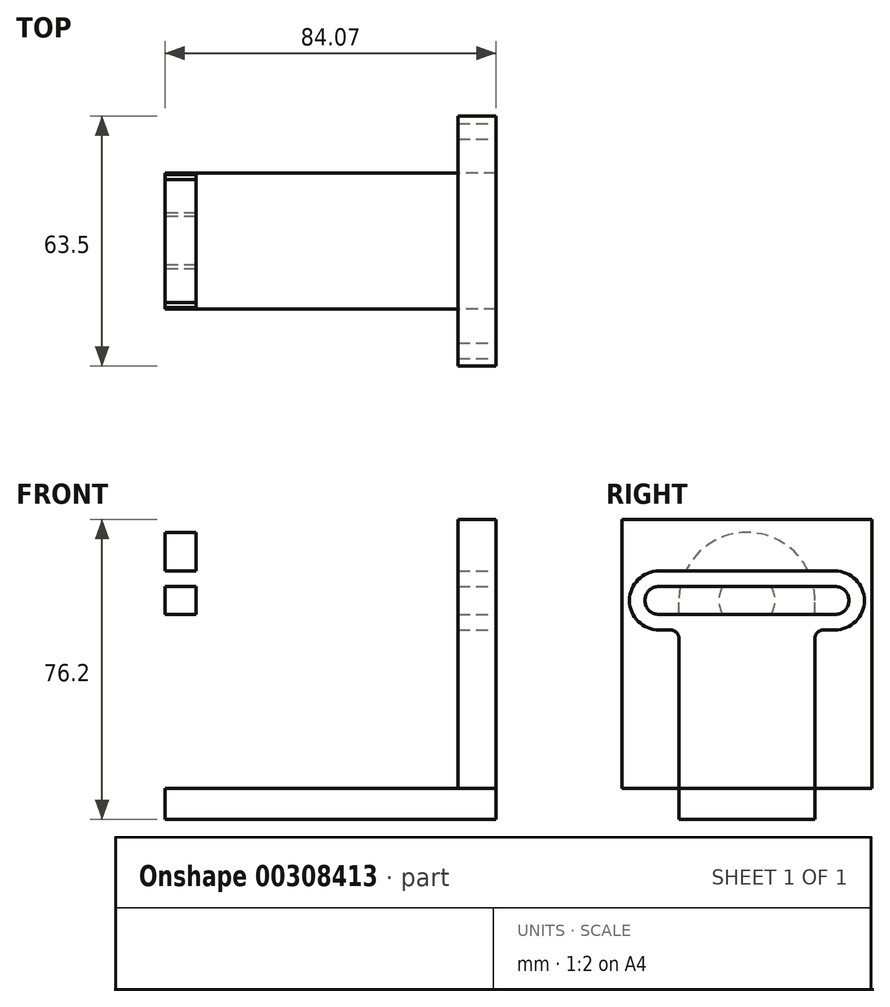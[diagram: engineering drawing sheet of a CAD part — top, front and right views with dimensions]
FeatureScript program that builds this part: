
annotation { "Feature Type Name" : "Feature", "Feature Type Description" : "" }
export const myFeature = defineFeature(function(context is Context, id is Id, definition is map)
    precondition{}
    {
        {
            var Q0;
            Q0=qCreatedBy(makeId("Front.planeOp"),FACE);
            var sketch = newSketch(context, id + "F0", { "sketchPlane" : qUnion([Q0])});
            skLineSegment(sketch, "E0.bottom", {"start": v(0, 0) * mm, "end": v(84.07, 0) * mm});
            skLineSegment(sketch, "E0.top", {"start": v(0, 76.2) * mm, "end": v(84.07, 76.2) * mm});
            skLineSegment(sketch, "E0.left", {"start": v(0, 0) * mm, "end": v(0, 76.2) * mm});
            skLineSegment(sketch, "E0.right", {"start": v(84.07, 0) * mm, "end": v(84.07, 76.2) * mm});
            skSolve(sketch);
        }
        {
            var Q0;
            Q0 = qSketchRegion(id + "F0", true);
            extrude(context, id + "F1", {"entities" : qUnion([Q0]), "oppositeDirection" : true, "depth" : 63.5 * mm});
        }
        {
            var Q0;
            Q0=makeQuery(id+"F1.opExtrude","CAP_FACE",FACE,{"disambiguationData":[OSD([sQuery(id+"F0.wireOp",EDGE,"E0.bottom"),sQuery(id+"F0.wireOp",EDGE,"E0.top"),sQuery(id+"F0.wireOp",EDGE,"E0.left"),sQuery(id+"F0.wireOp",EDGE,"E0.right")])],"isStart":true});
            var sketch = newSketch(context, id + "F2", { "sketchPlane" : qUnion([Q0])});
            skLineSegment(sketch, "E1", {"start": v(7.87, 76.2) * mm, "end": v(7.87, 7.87) * mm});
            skLineSegment(sketch, "E2", {"start": v(7.87, 7.87) * mm, "end": v(74.42, 7.87) * mm});
            skLineSegment(sketch, "E3", {"start": v(74.42, 7.87) * mm, "end": v(74.42, 76.2) * mm});
            skSolve(sketch);
        }
        {
            var Q0;
            {var subQ0=sQuery(id+"F2.wireOp",EDGE,"E1");Q0=makeQuery(id+"F2.imprint","IMPRINT",FACE,{"disambiguationData":[TD([[makeQuery(id+"F2.imprint","IMPRINT",EDGE,{"derivedFrom":subQ0}),1.0]])]});}
            extrude(context, id + "F3", {"entities" : qUnion([Q0]), "operationType" : NewBodyOperationType.REMOVE, "endBound" : BoundingType.THROUGH_ALL, "oppositeDirection" : true, "depth" : 25.4 * mm});
        }
        {
            var Q0;
            Q0=makeQuery(id+"F1.opExtrude","SWEPT_FACE",FACE,{"disambiguationData":[OSD([sQuery(id+"F0.wireOp",EDGE,"E0.left")])]});
            var sketch = newSketch(context, id + "F4", { "sketchPlane" : qUnion([Q0])});
            skLineSegment(sketch, "E4", {"start": v(-49.02, 7.87) * mm, "end": v(-14.48, 7.87) * mm});
            skLineSegment(sketch, "E5", {"start": v(-63.5, 7.87) * mm, "end": v(0, 7.87) * mm});
            skLineSegment(sketch, "E6", {"start": v(-31.75, 76.2) * mm, "end": v(-31.75, 7.87) * mm, "construction": true});
            skLineSegment(sketch, "E7", {"start": v(-49.02, 7.87) * mm, "end": v(-49.02, 55.63) * mm});
            skLineSegment(sketch, "E8", {"start": v(-14.48, 7.87) * mm, "end": v(-14.48, 55.63) * mm});
            skArc(sketch, "E9", {"start": v(-14.48, 55.63) * mm, "mid": v(-31.75, 72.9) * mm, "end": v(-49.02, 55.63) * mm});
            skCircle(sketch, "E10", {"center": v(-31.75, 55.63) * mm, "radius": 7.11 * mm});
            skCircle(sketch, "E11", {"center": v(-31.75, 36.58) * mm, "radius": 7.11 * mm});
            skLineSegment(sketch, "E12", {"start": v(-49.02, 7.87) * mm, "end": v(-49.02, 0) * mm});
            skLineSegment(sketch, "E13", {"start": v(-14.48, 7.87) * mm, "end": v(-14.48, 0) * mm});
            skSolve(sketch);
        }
        {
            var Q0;
            {var subQ1=sQuery(id+"F4.wireOp",EDGE,"E7");Q0=makeQuery(id+"F4.imprint","IMPRINT",FACE,{"disambiguationData":[TD([[makeQuery(id+"F4.imprint","IMPRINT",EDGE,{"derivedFrom":subQ1}),1.0]])]});}
            extrude(context, id + "F5", {"entities" : qUnion([Q0]), "operationType" : NewBodyOperationType.REMOVE, "oppositeDirection" : true, "depth" : 25.4 * mm});
        }
        {
            var Q0;
            {var subQ4=sQuery(id+"F4.wireOp",EDGE,"E12");Q0=makeQuery(id+"F4.imprint","IMPRINT",FACE,{"disambiguationData":[TD([[makeQuery(id+"F4.imprint","IMPRINT",EDGE,{"derivedFrom":subQ4}),-1.0]])]});}
            var Q1;
            {var subQ4=sQuery(id+"F4.wireOp",EDGE,"E13");Q1=makeQuery(id+"F4.imprint","IMPRINT",FACE,{"disambiguationData":[TD([[makeQuery(id+"F4.imprint","IMPRINT",EDGE,{"derivedFrom":subQ4}),1.0]])]});}
            extrude(context, id + "F6", {"entities" : qUnion([Q0, Q1]), "operationType" : NewBodyOperationType.REMOVE, "endBound" : BoundingType.THROUGH_ALL, "oppositeDirection" : true, "depth" : 25.4 * mm});
        }
        {
            var Q0;
            Q0=makeQuery(id+"F4.imprint","IMPRINT",FACE,{"disambiguationData":[TD([[makeQuery(id+"F4.imprint","IMPRINT",EDGE,{"derivedFrom":sQuery(id+"F4.wireOp",EDGE,"E11")}),1.0]])]});
            var Q1;
            Q1=makeQuery(id+"F4.imprint","IMPRINT",FACE,{"disambiguationData":[TD([[makeQuery(id+"F4.imprint","IMPRINT",EDGE,{"derivedFrom":sQuery(id+"F4.wireOp",EDGE,"E10")}),1.0]])]});
            extrude(context, id + "F7", {"entities" : qUnion([Q0, Q1]), "operationType" : NewBodyOperationType.REMOVE, "oppositeDirection" : true, "depth" : 25.4 * mm});
        }
        {
            var Q0;
            Q0=makeQuery(id+"F1.opExtrude","SWEPT_FACE",FACE,{"disambiguationData":[OSD([sQuery(id+"F0.wireOp",EDGE,"E0.right")])]});
            var sketch = newSketch(context, id + "F8", { "sketchPlane" : qUnion([Q0])});
            skLineSegment(sketch, "E14", {"start": v(14.48, 7.87) * mm, "end": v(49.02, 7.87) * mm});
            skLineSegment(sketch, "E15", {"start": v(31.75, 76.2) * mm, "end": v(31.75, 7.87) * mm, "construction": true});
            skLineSegment(sketch, "E16", {"start": v(31.75, 55.63) * mm, "end": v(9.4, 55.63) * mm, "construction": true});
            skLineSegment(sketch, "E17", {"start": v(31.75, 55.63) * mm, "end": v(54.1, 55.63) * mm, "construction": true});
            skArc(sketch, "E18.0.endCap", {"start": v(54.1, 59.18) * mm, "mid": v(57.66, 55.63) * mm, "end": v(54.1, 52.07) * mm});
            skLineSegment(sketch, "E18.0.left", {"start": v(31.75, 59.18) * mm, "end": v(54.1, 59.18) * mm});
            skLineSegment(sketch, "E18.0.right", {"start": v(31.75, 52.07) * mm, "end": v(54.1, 52.07) * mm});
            skArc(sketch, "E18.1.endCap", {"start": v(9.4, 52.07) * mm, "mid": v(5.84, 55.63) * mm, "end": v(9.4, 59.18) * mm});
            skLineSegment(sketch, "E18.1.left", {"start": v(31.75, 52.07) * mm, "end": v(9.4, 52.07) * mm});
            skLineSegment(sketch, "E18.1.right", {"start": v(31.75, 59.18) * mm, "end": v(9.4, 59.18) * mm});
            skArc(sketch, "E19.0.endCap", {"start": v(54.1, 63.1) * mm, "mid": v(61.58, 55.63) * mm, "end": v(54.1, 48.15) * mm});
            skLineSegment(sketch, "E19.0.left", {"start": v(31.75, 63.1) * mm, "end": v(54.1, 63.1) * mm});
            skLineSegment(sketch, "E19.0.right", {"start": v(51.2, 48.15) * mm, "end": v(54.1, 48.15) * mm});
            skArc(sketch, "E19.1.endCap", {"start": v(9.4, 48.15) * mm, "mid": v(1.92, 55.63) * mm, "end": v(9.4, 63.1) * mm});
            skLineSegment(sketch, "E19.1.left", {"start": v(12.3, 48.15) * mm, "end": v(9.4, 48.15) * mm});
            skLineSegment(sketch, "E19.1.right", {"start": v(31.75, 63.1) * mm, "end": v(9.4, 63.1) * mm});
            skArc(sketch, "E20.filletArc", {"start": v(14.48, 45.97) * mm, "mid": v(13.84, 47.51) * mm, "end": v(12.3, 48.15) * mm});
            skArc(sketch, "E21.filletArc", {"start": v(51.2, 48.15) * mm, "mid": v(49.66, 47.51) * mm, "end": v(49.02, 45.97) * mm});
            skLineSegment(sketch, "E22", {"start": v(14.48, 45.97) * mm, "end": v(14.48, 7.87) * mm});
            skLineSegment(sketch, "E23", {"start": v(49.02, 45.97) * mm, "end": v(49.02, 7.87) * mm});
            skSolve(sketch);
        }
        {
            var Q0;
            Q0=makeQuery(id+"F8.imprint","IMPRINT",FACE,{"disambiguationData":[TD([[makeQuery(id+"F8.imprint","IMPRINT",EDGE,{"derivedFrom":sQuery(id+"F8.wireOp",EDGE,"E19.0.endCap")}),1.0]])]});
            extrude(context, id + "F9", {"entities" : qUnion([Q0]), "operationType" : NewBodyOperationType.REMOVE, "endBound" : BoundingType.THROUGH_ALL, "oppositeDirection" : true, "depth" : 25.4 * mm});
        }
        {
            var Q0;
            Q0=makeQuery(id+"F8.imprint","IMPRINT",FACE,{"disambiguationData":[TD([[makeQuery(id+"F8.imprint","IMPRINT",EDGE,{"derivedFrom":sQuery(id+"F8.wireOp",EDGE,"E18.0.endCap")}),-1.0]])]});
            extrude(context, id + "F10", {"entities" : qUnion([Q0]), "operationType" : NewBodyOperationType.REMOVE, "oppositeDirection" : true, "depth" : 25.4 * mm});
        }
    });
